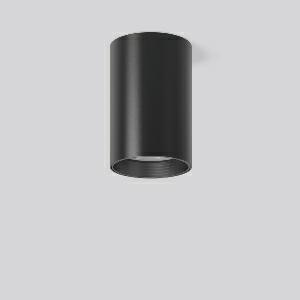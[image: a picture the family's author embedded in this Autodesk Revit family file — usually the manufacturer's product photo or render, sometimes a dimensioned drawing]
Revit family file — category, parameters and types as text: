
# Revit family: heledon_maxi_a_931221_003_76_d99f
name_source: partatom
category: Lighting Fixtures
units: mm (PartAtom-declared; Revit-internal decimal feet)

## family parameters
Cut with Voids When Loaded = No
Host = Face
Light Source = No
Part Type = Normal
Room Calculation Point = No
Round Connector Dimension = Use Diameter
Shared = No

## types (1)
- HELEDON maxi A (1 x LED Modul 930, 2750 lm, 3000)
    Apparent Load = 25 VA
    Approval mark = CE
    CIE Flux Codes = 96 100 100 100 100
    Color Rendering = 90
    Color Temperature = 3000
    Default Elevation = 1800 mm
    Description = Series: HELEDON maxi
Cylindrical surface-mounted downlight. Housing: die-cast aluminium, powder-coated. Internal ceiling frame polycarbonate with bayonet mounting. Black plastic ring and recessed LED to prevent glare from the side. Optical assembly with lens made of plastic (polycarbonate) for the best homogeneous light distribution - can be changed without tools. Best colour rendering index Ra>90. Suitable for Ceiling mounting. Easy installation with a separate ceiling frame with bayonet mounting and plug connection. Driver integrated. Connected via plug-in connector. High quality converter without flickering and stroboscopic effect. The following accessories can be mounted without use of tools: interchangeable lenses, decorative glasses, honeycomb louvre, clear and frosted diffusers, white interchangeable plastic ring. 
Colour: deep black, matt (RAL 9005)
Diameter: 123 mm
Height: 183 mm
Lamp: LED
Socket: without socket
Colour temperature: 3000K
Colour rendering index (CRI): 92
System power: 25 W
Rated luminous flux: 2750 lm
Luminous efficiency: 110 lm/W
Control gear: Converter, dimmable, DALI
Protection class: I
Type of protection: IP 20
    Height = 183 mm
    Lamp = 1 x LED Modul 930
    Lamp Light Flux = 2750 lm
    Lamp count = 1
    Length = 123 mm
    Lifetime = 50000 h
    Luminous efficacy = 110 lm/W
    Manufacturer = RZB
    ModVariant = No
    Model = 931221.003.76
    Mounting Place = Ceiling
    Mounting Type = Surface mounted
    Number of Poles = 1
    OnlyDefault = Yes
    Power Factor = 1
    Product Name = HELEDON maxi A
    Product group = Surface mounted downlights
    ProductGroupID = 302
    Protection Class = Protection class I
    Protection Degree = IP 20
    RLX_Detail_Level = 1
    RLX_Emergency_Light_Flux = 0 lm
    RLX_Emergency_Type = 0
    RLX_Emergency_Type_DB = No
    RlxData = <blob elided: 99669 chars, md5=7d0a412d>
    Socket = socket
    Standby Power = 0 W
    System Light Flux = 2750 lm
    System Power = 25 W
    Type Comments = Product without accessories
    Type Image = 931193.003.jpg
    URL = http://relux.com
    VarID = ---
    Voltage = 230 V
    Voltage Range = 220-240 V
    Weight = 0.00 kg
    Width = 0 mm  [stored 0 ft]

note: [stored X ft] marks values corroborated as IEEE doubles in the binary element streams (Revit-internal decimal feet)

## geometry (parser evidence)
native form markers: Blend x4, Sweep x11
no freeform markers — native parametric forms only
